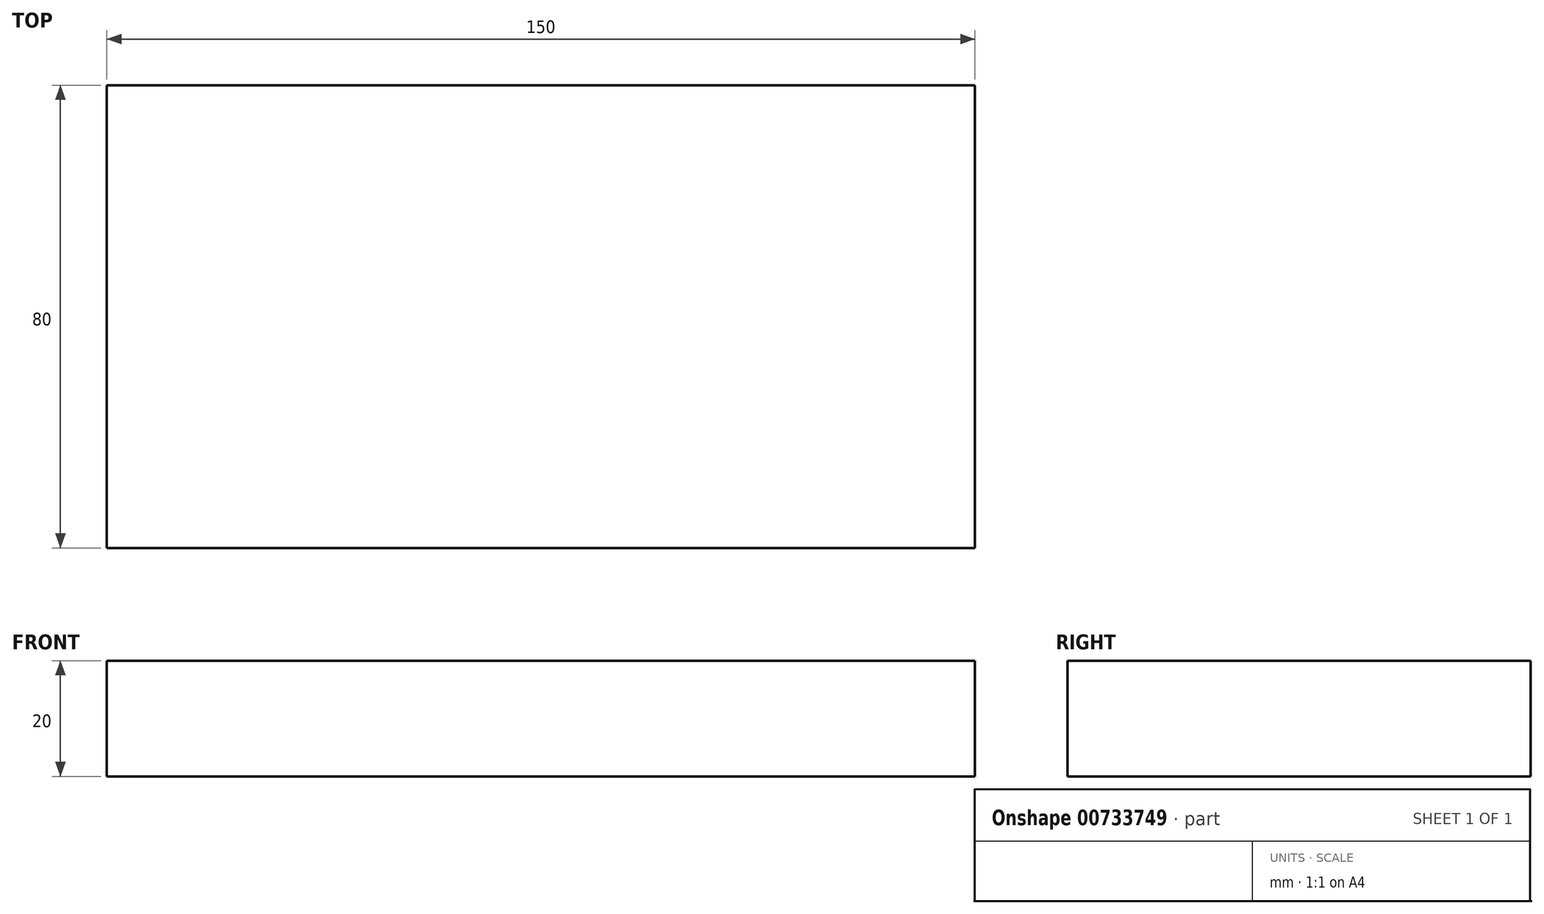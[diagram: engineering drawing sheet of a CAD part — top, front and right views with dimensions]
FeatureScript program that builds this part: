
annotation { "Feature Type Name" : "Feature", "Feature Type Description" : "" }
export const myFeature = defineFeature(function(context is Context, id is Id, definition is map)
    precondition{}
    {
        {
            var Q0;
            Q0=qCreatedBy(makeId("Top.planeOp"),FACE);
            var sketch = newSketch(context, id + "F0", { "sketchPlane" : qUnion([Q0])});
            skLineSegment(sketch, "E0.bottom", {"start": v(0, 0) * mm, "end": v(150, 0) * mm});
            skLineSegment(sketch, "E0.top", {"start": v(0, -80) * mm, "end": v(150, -80) * mm});
            skLineSegment(sketch, "E0.left", {"start": v(0, 0) * mm, "end": v(0, -80) * mm});
            skLineSegment(sketch, "E0.right", {"start": v(150, 0) * mm, "end": v(150, -80) * mm});
            skSolve(sketch);
        }
        {
            var Q0;
            Q0=makeQuery(id+"F0.imprint","IMPRINT",FACE,{"disambiguationData":[TD([[makeQuery(id+"F0.imprint","IMPRINT",EDGE,{"derivedFrom":sQuery(id+"F0.wireOp",EDGE,"E0.bottom")}),-1.0]])]});
            extrude(context, id + "F1", {"entities" : qUnion([Q0]), "depth" : 20 * mm, "offsetDistance" : 25 * mm});
        }
    });
